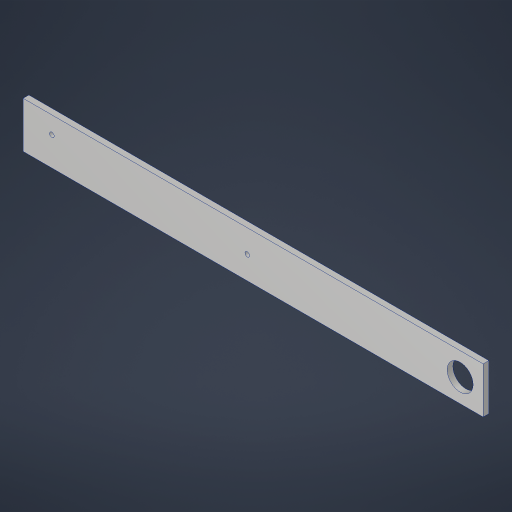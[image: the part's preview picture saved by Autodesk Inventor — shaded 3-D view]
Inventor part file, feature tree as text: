
AUTODESK INVENTOR PART (.ipt)
format: ipt  version: 2023.4 (Build 274418000, 418)  size: 187,392 bytes
history: native  units: in
note: dims shown in document units (in); Inventor stores cm internally (conversion verified against a paired STEP export)
features: sketch x1, extrude x1, hole x1
ambient origin geometry x8: Origin, YZ Plane, XZ Plane, XY Plane, X Axis, Y Axis, Z Axis, Center Point
bodies: Solid1 (feature_tree)
feature tree (3):
  sketch  "Sketch1"  dims[d0=20.0in d1=2.0in d3=1.125in d4=7.375in d5=24.0in d6=8.5in d7=0.25in d10=1.125in d11=1.0in d12=0.25in d13=0.0in d14=0.201in d15=0.75in d16=0.385in d17=0.25in d18=0.5635in d19=1.0in d20=0.8108in d26=1.25in d27=0.75in d28=1.125in]
  extrude  "Extrusion1"  Depth=2.0in
  hole  "Hole1"  [1 undecoded]
note: 1 required parameter value undecoded (feature->parameter linkage not recoverable at this tier; creation-order binding heuristic only, values carry confidence <= 0.55)
